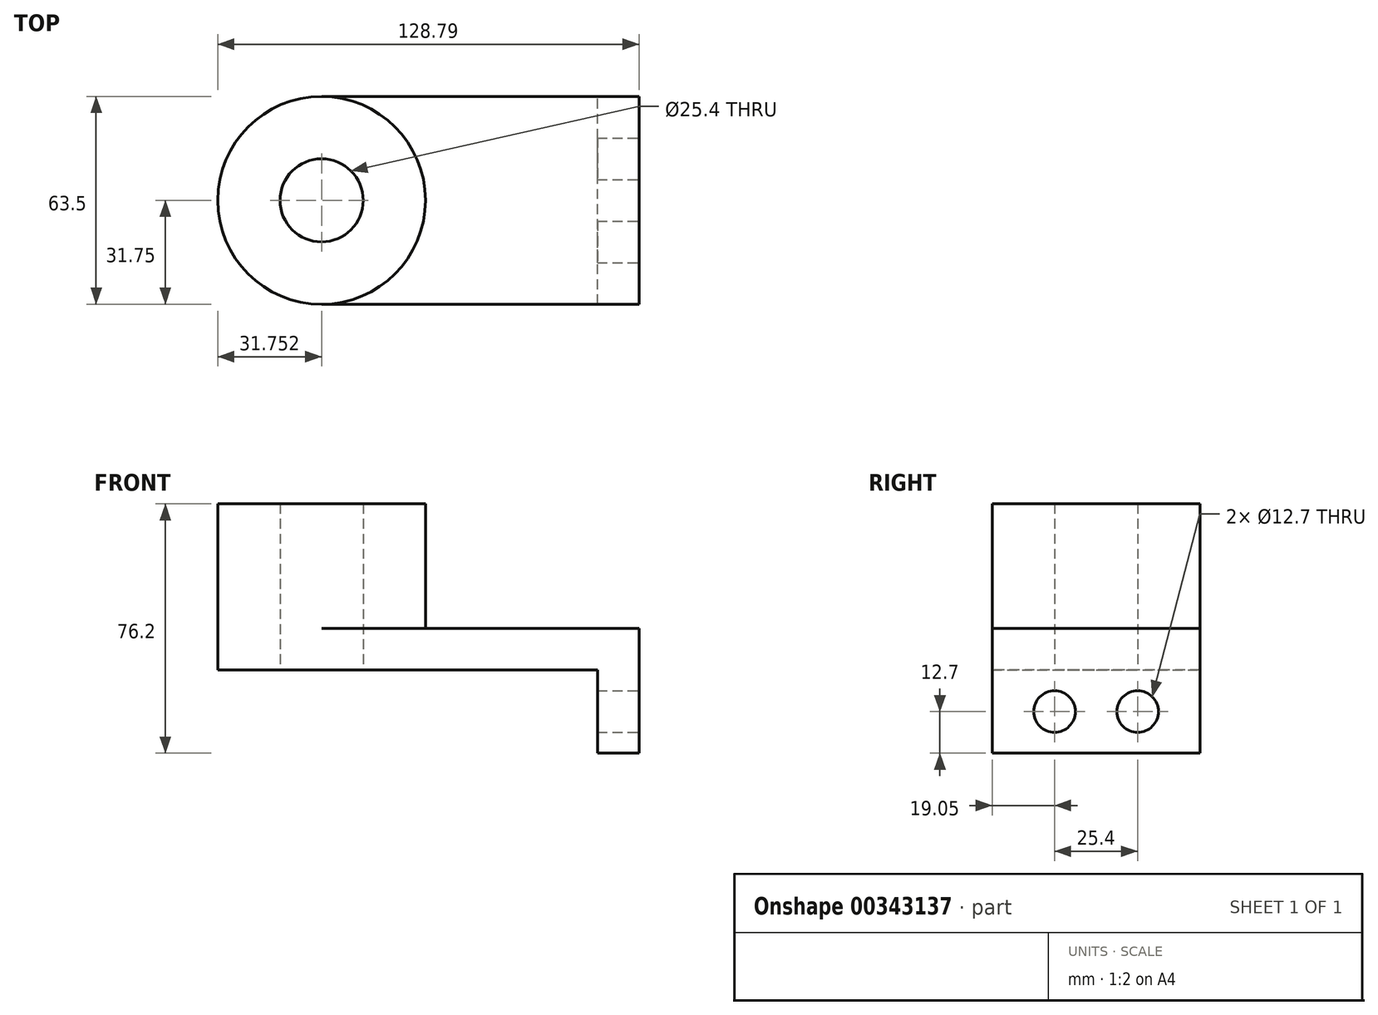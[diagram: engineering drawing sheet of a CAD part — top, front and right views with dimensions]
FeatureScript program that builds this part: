
annotation { "Feature Type Name" : "Feature", "Feature Type Description" : "" }
export const myFeature = defineFeature(function(context is Context, id is Id, definition is map)
    precondition{}
    {
        {
            var Q0;
            Q0=qCreatedBy(makeId("Top.planeOp"),FACE);
            var sketch = newSketch(context, id + "F0", { "sketchPlane" : qUnion([Q0])});
            skLineSegment(sketch, "E0.bottom", {"start": v(48.52, -31.75) * mm, "end": v(-48.52, -31.75) * mm});
            skLineSegment(sketch, "E0.top", {"start": v(48.52, 31.75) * mm, "end": v(-48.52, 31.75) * mm});
            skLineSegment(sketch, "E0.left", {"start": v(48.52, -31.75) * mm, "end": v(48.52, 31.75) * mm});
            skLineSegment(sketch, "E0.right", {"start": v(-48.52, -31.75) * mm, "end": v(-48.52, 31.75) * mm});
            skPoint(sketch, "E0.middle", {"position": v(0, 0) * mm});
            skCircle(sketch, "E1", {"center": v(-48.52, 0) * mm, "radius": 31.75 * mm});
            skCircle(sketch, "E2", {"center": v(-48.52, 0) * mm, "radius": 12.7 * mm});
            skSolve(sketch);
        }
        {
            var Q0;
            Q0 = qSketchRegion(id + "F0", true);
            extrude(context, id + "F1", {"entities" : qUnion([Q0]), "depth" : 12.7 * mm});
        }
        {
            var Q0;
            {var subQ1=sQuery(id+"F0.wireOp",EDGE,"E0.right");var subQ3=sQuery(id+"F0.wireOp",EDGE,"E2");var subQ4=makeQuery(id+"F0.imprint","INTERSECT",VERTEX,{"disambiguationData":[OD(0.0)],"derivedFrom":[subQ1,subQ3]});Q0=makeQuery(id+"F0.imprint","IMPRINT",FACE,{"disambiguationData":[TD([[makeQuery(id+"F0.imprint","IMPRINT",EDGE,{"disambiguationData":[TD([[subQ4,1.0]])],"derivedFrom":subQ3}),-1.0]])]});}
            var Q1;
            {var subQ1=sQuery(id+"F0.wireOp",EDGE,"E0.right");var subQ3=sQuery(id+"F0.wireOp",EDGE,"E2");var subQ4=makeQuery(id+"F0.imprint","INTERSECT",VERTEX,{"disambiguationData":[OD(0.0)],"derivedFrom":[subQ1,subQ3]});Q1=makeQuery(id+"F0.imprint","IMPRINT",FACE,{"disambiguationData":[TD([[makeQuery(id+"F0.imprint","IMPRINT",EDGE,{"disambiguationData":[TD([[subQ4,-1.0]])],"derivedFrom":subQ3}),-1.0]])]});}
            extrude(context, id + "F2", {"entities" : qUnion([Q0, Q1]), "operationType" : NewBodyOperationType.ADD, "depth" : 50.8 * mm});
        }
        {
            var Q0;
            Q0=makeQuery(id+"F1.opExtrude","SWEPT_FACE",FACE,{"disambiguationData":[OSD([sQuery(id+"F0.wireOp",EDGE,"E0.left")])]});
            var sketch = newSketch(context, id + "F3", { "sketchPlane" : qUnion([Q0])});
            skLineSegment(sketch, "E3.bottom", {"start": v(-31.75, 12.7) * mm, "end": v(31.75, 12.7) * mm});
            skLineSegment(sketch, "E3.top", {"start": v(-31.75, -25.4) * mm, "end": v(31.75, -25.4) * mm});
            skLineSegment(sketch, "E3.left", {"start": v(-31.75, 12.7) * mm, "end": v(-31.75, -25.4) * mm});
            skLineSegment(sketch, "E3.right", {"start": v(31.75, 12.7) * mm, "end": v(31.75, -25.4) * mm});
            skCircle(sketch, "E4", {"center": v(-12.7, -12.7) * mm, "radius": 6.35 * mm});
            skLineSegment(sketch, "E5", {"start": v(0, 0) * mm, "end": v(0, -25.4) * mm});
            skCircle(sketch, "E6.MirrorC", {"center": v(12.7, -12.7) * mm, "radius": 6.35 * mm});
            skSolve(sketch);
        }
        {
            var Q0;
            Q0 = qSketchRegion(id + "F3", true);
            extrude(context, id + "F4", {"entities" : qUnion([Q0]), "operationType" : NewBodyOperationType.ADD, "oppositeDirection" : true, "depth" : 12.7 * mm});
        }
    });
